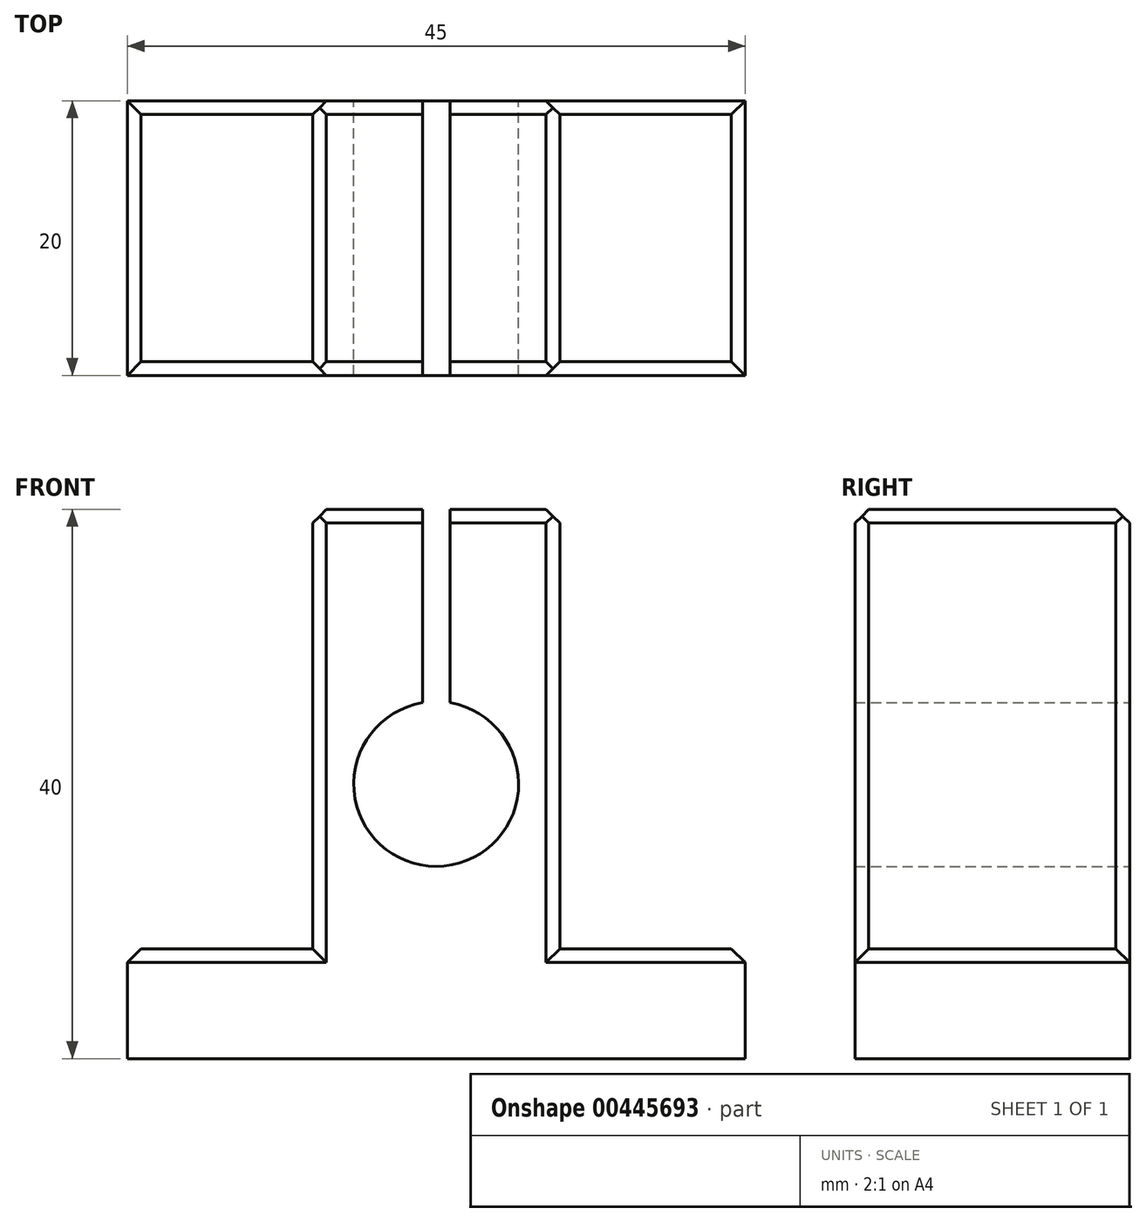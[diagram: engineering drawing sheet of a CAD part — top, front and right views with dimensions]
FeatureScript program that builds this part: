
annotation { "Feature Type Name" : "Feature", "Feature Type Description" : "" }
export const myFeature = defineFeature(function(context is Context, id is Id, definition is map)
    precondition{}
    {
        {
            var Q0;
            Q0=qCreatedBy(makeId("Front.planeOp"),FACE);
            var sketch = newSketch(context, id + "F0", { "sketchPlane" : qUnion([Q0])});
            skLineSegment(sketch, "E0.0", {"start": v(-22.5, -12) * mm, "end": v(-22.5, -20) * mm});
            skLineSegment(sketch, "E1.0", {"start": v(22.5, -12) * mm, "end": v(22.5, -20) * mm});
            skLineSegment(sketch, "E2.0", {"start": v(-22.5, -20) * mm, "end": v(22.5, -20) * mm});
            skLineSegment(sketch, "E3.0", {"start": v(-9, 20) * mm, "end": v(-1, 20) * mm});
            skPoint(sketch, "E4.orphan", {"position": v(0, 61.41) * mm});
            skPoint(sketch, "E5.orphan", {"position": v(-66, 0) * mm});
            skLineSegment(sketch, "E6.0", {"start": v(-9, 20) * mm, "end": v(-9, -12) * mm});
            skLineSegment(sketch, "E7.0", {"start": v(9, 20) * mm, "end": v(9, -12) * mm});
            skLineSegment(sketch, "E8.0", {"start": v(-22.5, -12) * mm, "end": v(-9, -12) * mm});
            skLineSegment(sketch, "E9.trimOffspring", {"start": v(9, -12) * mm, "end": v(22.5, -12) * mm});
            skArc(sketch, "E10", {"start": v(-1, 5.92) * mm, "mid": v(0, -6) * mm, "end": v(1, 5.92) * mm});
            skLineSegment(sketch, "E11.0", {"start": v(-1, 20) * mm, "end": v(-1, 5.92) * mm});
            skLineSegment(sketch, "E12.0", {"start": v(1, 20) * mm, "end": v(1, 5.92) * mm});
            skPoint(sketch, "E13.orphan", {"position": v(0, 33.4) * mm});
            skLineSegment(sketch, "E14.trimOffspring", {"start": v(1, 20) * mm, "end": v(9, 20) * mm});
            skSolve(sketch);
        }
        {
            var Q0;
            Q0 = qSketchRegion(id + "F0", true);
            extrude(context, id + "F1", {"entities" : qUnion([Q0]), "depth" : 20 * mm});
        }
        {
            var Q0;
            Q0=makeQuery(id+"F1.opExtrude","CAP_EDGE",EDGE,{"disambiguationData":[OSD([sQuery(id+"F0.wireOp",EDGE,"E3.0")])],"isStart":false});
            var Q1;
            Q1=makeQuery(id+"F1.opExtrude","CAP_EDGE",EDGE,{"disambiguationData":[OSD([sQuery(id+"F0.wireOp",EDGE,"E3.0")])],"isStart":true});
            var Q2;
            Q2=makeQuery(id+"F1.opExtrude","CAP_EDGE",EDGE,{"disambiguationData":[OSD([sQuery(id+"F0.wireOp",EDGE,"E14.trimOffspring")])],"isStart":true});
            var Q3;
            Q3=makeQuery(id+"F1.opExtrude","CAP_EDGE",EDGE,{"disambiguationData":[OSD([sQuery(id+"F0.wireOp",EDGE,"E14.trimOffspring")])],"isStart":false});
            var Q4;
            Q4=makeQuery(id+"F1.opExtrude","SWEPT_EDGE",EDGE,{"disambiguationData":[OSD([sQuery(id+"F0.wireOp",EDGE,"E7.0"),sQuery(id+"F0.wireOp",EDGE,"E14.trimOffspring")])]});
            var Q5;
            Q5=makeQuery(id+"F1.opExtrude","SWEPT_EDGE",EDGE,{"disambiguationData":[OSD([sQuery(id+"F0.wireOp",EDGE,"E3.0"),sQuery(id+"F0.wireOp",EDGE,"E6.0")])]});
            chamfer(context, id + "F2", {"entities" : qUnion([Q0, Q1, Q2, Q3, Q4, Q5]), "width" : 1 * mm, "tangentPropagation" : true});
        }
        {
            var Q0;
            Q0=makeQuery(id+"F1.opExtrude","CAP_EDGE",EDGE,{"disambiguationData":[OSD([sQuery(id+"F0.wireOp",EDGE,"E9.trimOffspring")])],"isStart":true});
            var Q1;
            Q1=makeQuery(id+"F1.opExtrude","CAP_EDGE",EDGE,{"disambiguationData":[OSD([sQuery(id+"F0.wireOp",EDGE,"E9.trimOffspring")])],"isStart":false});
            var Q2;
            Q2=makeQuery(id+"F1.opExtrude","SWEPT_EDGE",EDGE,{"disambiguationData":[OSD([sQuery(id+"F0.wireOp",EDGE,"E1.0"),sQuery(id+"F0.wireOp",EDGE,"E9.trimOffspring")])]});
            var Q3;
            Q3=makeQuery(id+"F1.opExtrude","CAP_EDGE",EDGE,{"disambiguationData":[OSD([sQuery(id+"F0.wireOp",EDGE,"E8.0")])],"isStart":false});
            var Q4;
            Q4=makeQuery(id+"F1.opExtrude","SWEPT_EDGE",EDGE,{"disambiguationData":[OSD([sQuery(id+"F0.wireOp",EDGE,"E0.0"),sQuery(id+"F0.wireOp",EDGE,"E8.0")])]});
            var Q5;
            Q5=makeQuery(id+"F1.opExtrude","CAP_EDGE",EDGE,{"disambiguationData":[OSD([sQuery(id+"F0.wireOp",EDGE,"E8.0")])],"isStart":true});
            chamfer(context, id + "F3", {"entities" : qUnion([Q0, Q1, Q2, Q3, Q4, Q5]), "width" : 1 * mm, "tangentPropagation" : true});
        }
        {
            var Q0;
            Q0=makeQuery(id+"F1.opExtrude","CAP_EDGE",EDGE,{"disambiguationData":[OSD([sQuery(id+"F0.wireOp",EDGE,"E7.0")])],"isStart":true});
            var Q1;
            Q1=makeQuery(id+"F1.opExtrude","CAP_EDGE",EDGE,{"disambiguationData":[OSD([sQuery(id+"F0.wireOp",EDGE,"E6.0")])],"isStart":true});
            var Q2;
            Q2=makeQuery(id+"F1.opExtrude","CAP_EDGE",EDGE,{"disambiguationData":[OSD([sQuery(id+"F0.wireOp",EDGE,"E7.0")])],"isStart":false});
            var Q3;
            Q3=makeQuery(id+"F1.opExtrude","CAP_EDGE",EDGE,{"disambiguationData":[OSD([sQuery(id+"F0.wireOp",EDGE,"E6.0")])],"isStart":false});
            chamfer(context, id + "F4", {"entities" : qUnion([Q0, Q1, Q2, Q3]), "width" : 1 * mm, "tangentPropagation" : true});
        }
    });
